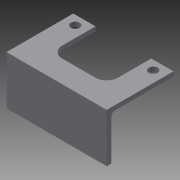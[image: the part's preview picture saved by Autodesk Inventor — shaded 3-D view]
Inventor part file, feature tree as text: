
AUTODESK INVENTOR PART (.ipt)
format: ipt  version: 2015 (Build 190159000, 159)  size: 106,496 bytes
history: native  units: mm
features: extrude x2, fillet x2, sketch x2
ambient origin geometry x8: Origin, YZ Plane, XZ Plane, XY Plane, X Axis, Y Axis, Z Axis, Center Point
bodies: Solid1 (feature_tree)
feature tree (6):
  extrude  "Extrusion1"  Depth=10.0mm
  fillet  "Fillet1"  Radius=10.0mm
  extrude  "Extrusion2"  Depth=30.0mm
  fillet  "Fillet2"  Radius=4.0mm
  sketch  "Sketch1"  dims[d0=45.0mm d1=10.0mm d2=10.0mm]
  sketch  "Sketch2"  dims[d3=10.0mm d4=30.0mm d5=4.0mm d6=4.0mm d7=2.0mm d8=0.0mm d9=5.0mm d10=2.0mm d11=20.0mm d12=0.0mm d13=2.0mm]
